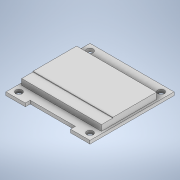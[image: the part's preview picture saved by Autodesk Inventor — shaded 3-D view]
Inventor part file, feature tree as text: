
AUTODESK INVENTOR PART (.ipt)
format: ipt  version: 2022 (Build 260153000, 153)  size: 137,216 bytes
history: native  units: mm
features: extrude x4, sketch x2, other x1
ambient origin geometry x8: Origin, YZ Plane, XZ Plane, XY Plane, X Axis, Y Axis, Z Axis, Center Point
bodies: Body1 (feature_tree)
feature tree (7):
  other  "솔리드1"
  sketch  "스케치1"
  extrude  "돌출1"  Depth=26.0mm
  extrude  "돌출3"  Depth=26.0mm
  extrude  "돌출4"  Depth=2.0mm
  extrude  "돌출5"  Depth=2.0mm
  sketch  "스케치2"
